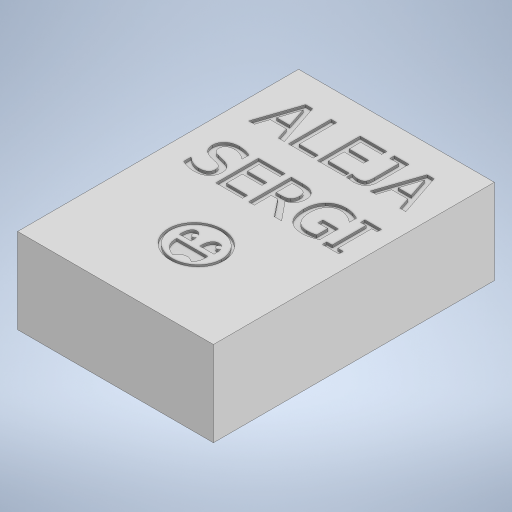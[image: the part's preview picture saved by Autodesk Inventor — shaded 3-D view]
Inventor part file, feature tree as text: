
AUTODESK INVENTOR PART (.ipt)
format: ipt  version: 2024 (Build 280153000, 153)  size: 448,000 bytes
history: native  units: mm
features: sketch x3, extrude x2, other x1
ambient origin geometry x8: Origin, YZ Plane, XZ Plane, XY Plane, X Axis, Y Axis, Z Axis, Center Point
bodies: Body1 (feature_tree)
feature tree (6):
  extrude  "Extrusión2"  Depth=230.0mm
  sketch  "Boceto3"  dims[d5=100.0mm d6=0.0mm d13=3.0mm d14=0.0mm]
  extrude  "Extrusión3"  Depth=3.0mm TaperAngle=0.0deg
  other  "Repujado1"
  sketch  "Boceto2"  dims[d3=330.0mm d4=230.0mm]
  sketch  "Boceto4"  dims[d15=3.0mm d16=0.0mm]
